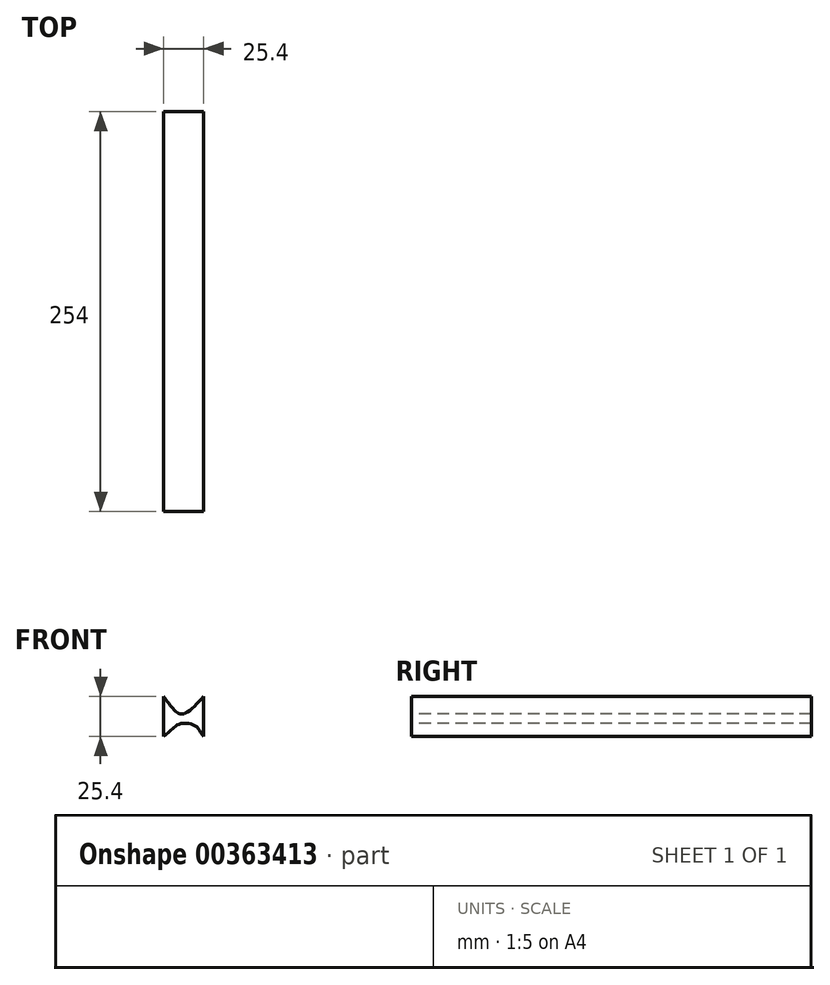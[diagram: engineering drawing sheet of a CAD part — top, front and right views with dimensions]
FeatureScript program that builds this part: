
annotation { "Feature Type Name" : "Feature", "Feature Type Description" : "" }
export const myFeature = defineFeature(function(context is Context, id is Id, definition is map)
    precondition{}
    {
        {
            var Q0;
            Q0=qCreatedBy(makeId("Front.planeOp"),FACE);
            var sketch = newSketch(context, id + "F0", { "sketchPlane" : qUnion([Q0])});
            skLineSegment(sketch, "E0.bottom", {"start": v(0, 0) * mm, "end": v(25.4, 0) * mm});
            skLineSegment(sketch, "E0.top", {"start": v(0, -25.4) * mm, "end": v(25.4, -25.4) * mm});
            skLineSegment(sketch, "E0.left", {"start": v(0, 0) * mm, "end": v(0, -25.4) * mm});
            skLineSegment(sketch, "E0.right", {"start": v(25.4, 0) * mm, "end": v(25.4, -25.4) * mm});
            skSolve(sketch);
        }
        {
            var Q0;
            Q0 = qSketchRegion(id + "F0", true);
            extrude(context, id + "F1", {"entities" : qUnion([Q0]), "depth" : 254 * mm});
        }
        {
            var Q0;
            Q0=makeQuery(id+"F1.opExtrude","CAP_FACE",FACE,{"disambiguationData":[OSD([sQuery(id+"F0.wireOp",EDGE,"E0.bottom"),sQuery(id+"F0.wireOp",EDGE,"E0.top"),sQuery(id+"F0.wireOp",EDGE,"E0.left"),sQuery(id+"F0.wireOp",EDGE,"E0.right")])],"isStart":false});
            var sketch = newSketch(context, id + "F2", { "sketchPlane" : qUnion([Q0])});
            skFitSpline(sketch, "E1", {"points": [v(0, 0) * mm, v(6.07, -7.92) * mm, v(12.01, -11.15) * mm, v(25.4, 0) * mm], "startDerivative": vector(18.55, -26.38) * mm, "endDerivative": vector(34.55, 38.13) * mm});
            skFitSpline(sketch, "E2", {"points": [v(0, 0) * mm, v(-1.4, 10.51) * mm, v(11.73, 11.14) * mm, v(27.91, 12.08) * mm, v(25.4, 0) * mm], "startDerivative": vector(-19.47, 58.7) * mm, "endDerivative": vector(-26.84, -63.82) * mm});
            skFitSpline(sketch, "E3", {"points": [v(0, -25.4) * mm, v(4.87, -21.18) * mm, v(10.65, -17.37) * mm, v(19.9, -18.57) * mm, v(25.4, -25.4) * mm, v(34.78, -37.7) * mm, v(31.68, -46.95) * mm, v(11.2, -51.94) * mm, v(6.13, -51.8) * mm, v(-2.5, -51.88) * mm, v(-8.64, -49.13) * mm, v(-16.53, -46.95) * mm, v(-18.2, -43.5) * mm, v(-17.92, -39.92) * mm, v(-15.46, -35.39) * mm, v(-6, -29.32) * mm, v(0, -25.4) * mm]});
            skSolve(sketch);
        }
        {
            var Q0;
            Q0=makeQuery(id+"F2.imprint","IMPRINT",FACE,{"disambiguationData":[TD([[makeQuery(id+"F2.imprint","IMPRINT",EDGE,{"derivedFrom":sQuery(id+"F2.wireOp",EDGE,"E1")}),1.0]])]});
            var Q1;
            Q1=makeQuery(id+"F2.imprint","IMPRINT",FACE,{"disambiguationData":[TD([[makeQuery(id+"F2.imprint","IMPRINT",EDGE,{"derivedFrom":sQuery(id+"F2.wireOp",EDGE,"E2")}),-1.0]])]});
            var Q2;
            {var subQ1=makeQuery(id+"F1.opExtrude","CAP_EDGE",EDGE,{"disambiguationData":[OSD([sQuery(id+"F0.wireOp",EDGE,"E0.top")])],"isStart":false});Q2=makeQuery(id+"F2.imprint","IMPRINT",FACE,{"disambiguationData":[TD([[makeQuery(id+"F2.imprint","IMPRINT",EDGE,{"derivedFrom":subQ1}),1.0]])]});}
            var Q3;
            {var subQ1=makeQuery(id+"F1.opExtrude","CAP_EDGE",EDGE,{"disambiguationData":[OSD([sQuery(id+"F0.wireOp",EDGE,"E0.top")])],"isStart":false});Q3=makeQuery(id+"F2.imprint","IMPRINT",FACE,{"disambiguationData":[TD([[makeQuery(id+"F2.imprint","IMPRINT",EDGE,{"derivedFrom":subQ1}),-1.0]])]});}
            extrude(context, id + "F3", {"entities" : qUnion([Q0, Q1, Q2, Q3]), "operationType" : NewBodyOperationType.REMOVE, "endBound" : BoundingType.THROUGH_ALL, "oppositeDirection" : true, "depth" : 25.4 * mm});
        }
    });
